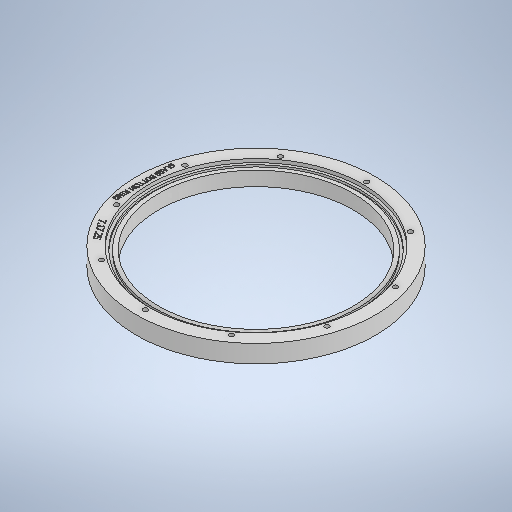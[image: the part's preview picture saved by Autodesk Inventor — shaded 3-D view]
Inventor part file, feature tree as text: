
AUTODESK INVENTOR PART (.ipt)
format: ipt  version: 2025 (Build 290162000, 162)  size: 755,200 bytes
history: native  units: mm
features: sketch x6, extrude x3, emboss x2, hole x1, pattern_circular x1
ambient origin geometry x8: Origin, YZ Plane, XZ Plane, XY Plane, X Axis, Y Axis, Z Axis, Center Point
bodies: Solid1 (feature_tree)
feature tree (13):
  extrude  "Ring"  Depth=270.0mm
  extrude  "Glass Seat"  Depth=241.0mm
  hole  "Holes"  [1 undecoded]
  pattern_circular  "Circular Pattern1"  Count=10 Angle=360.0deg
  emboss  "Emboss1"
  extrude  "Seal Groove"  Depth=2.5mm TaperAngle=0.0deg
  emboss  "Emboss2"
  sketch  "Sketch1"  dims[d0=220.0mm d1=270.0mm]
  sketch  "Sketch2"  dims[d2=20.0mm d3=0.0mm d4=241.0mm]
  sketch  "Sketch3"  dims[d5=3.9mm d6=0.0mm]
  sketch  "Sketch4"  dims[d7=5.2mm d8=6.0mm d9=4.0mm d10=2.0mm d11=90.0deg d12=8.0mm d13=20.594885mm d14=125.0mm d15=100.0mm d16=360.0deg]
  sketch  "Sketch5"  dims[d18=1.0mm d19=0.0mm d23=2.5mm d24=0.0mm]
  sketch  "Sketch6"  dims[d25=3.0mm d26=3.0mm d27=1.0mm d28=0.0mm]
note: 1 required parameter value undecoded (feature->parameter linkage not recoverable at this tier; creation-order binding heuristic only, values carry confidence <= 0.55)
